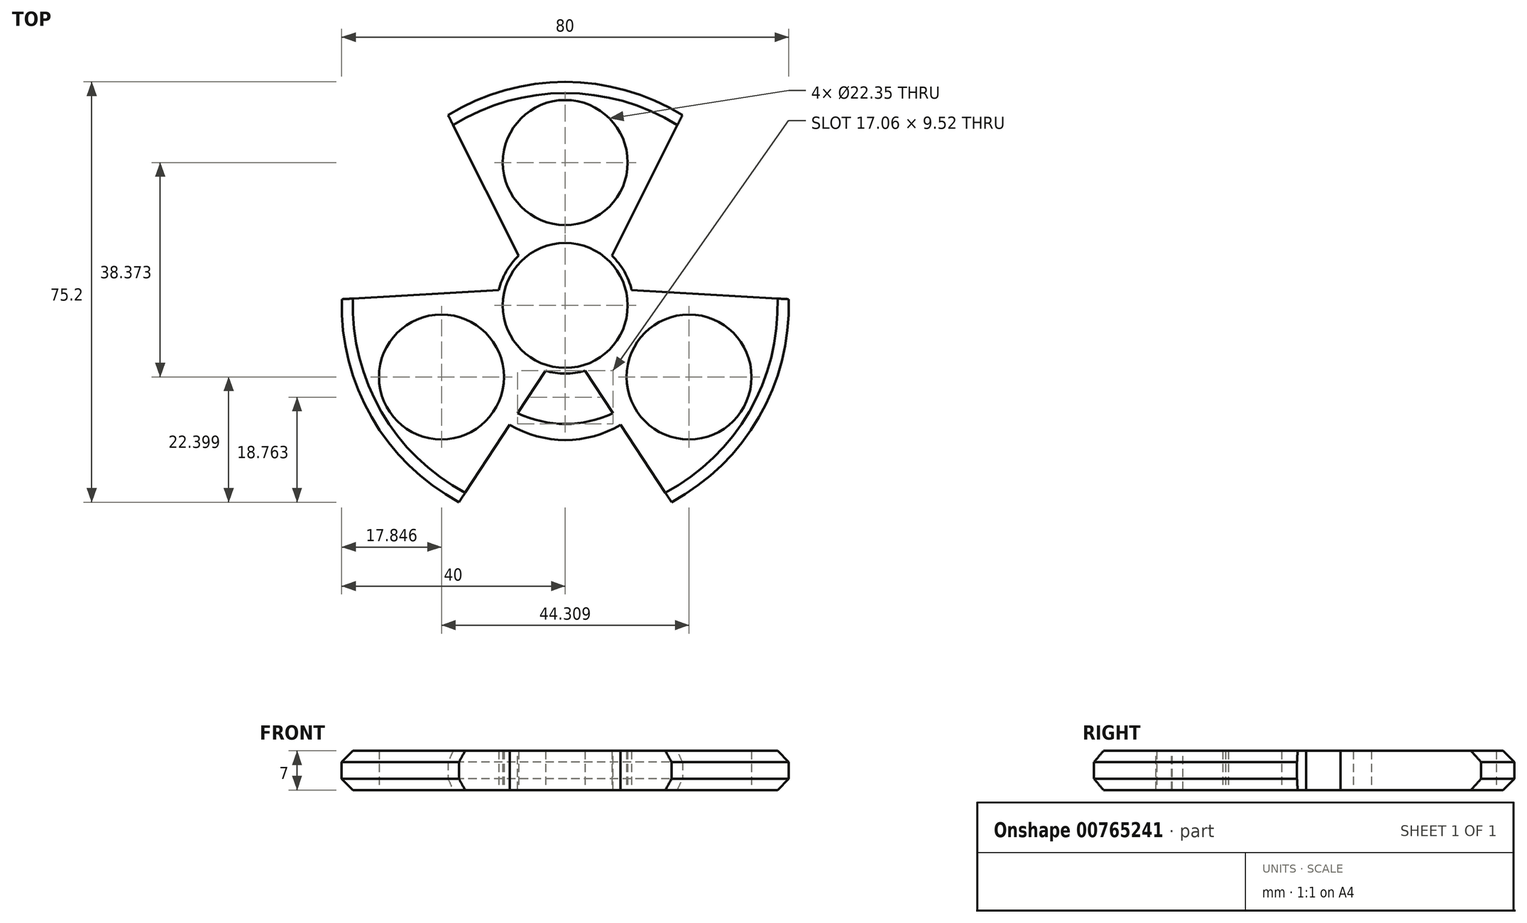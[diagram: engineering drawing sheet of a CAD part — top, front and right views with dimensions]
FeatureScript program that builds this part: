
annotation { "Feature Type Name" : "Feature", "Feature Type Description" : "" }
export const myFeature = defineFeature(function(context is Context, id is Id, definition is map)
    precondition{}
    {
        {
            var Q0;
            Q0=qCreatedBy(makeId("Top.planeOp"),FACE);
            var sketch = newSketch(context, id + "F0", { "sketchPlane" : qUnion([Q0])});
            skCircle(sketch, "E0", {"center": v(0, 0) * mm, "radius": 11.18 * mm});
            skCircle(sketch, "E1", {"center": v(0, 25.58) * mm, "radius": 11.18 * mm});
            skCircle(sketch, "E2", {"center": v(0, 0) * mm, "radius": 12.2 * mm});
            skLineSegment(sketch, "E3", {"start": v(-8.34, 8.9) * mm, "end": v(-20.97, 34.07) * mm});
            skLineSegment(sketch, "E4.MirrorCS", {"start": v(8.34, 8.9) * mm, "end": v(20.97, 34.07) * mm});
            skArc(sketch, "E5", {"start": v(20.97, 34.07) * mm, "mid": v(0, 40) * mm, "end": v(-20.97, 34.07) * mm});
            skSolve(sketch);
        }
        {
            var Q0;
            Q0 = qSketchRegion(id + "F0", true);
            extrude(context, id + "F1", {"entities" : qUnion([Q0]), "depth" : 7 * mm, "offsetDistance" : 25.4 * mm});
        }
        {
            var Q0;
            Q0=makeQuery(id+"F1.opExtrude","SWEPT_BODY",BODY,{"disambiguationData":[OSD([sQuery(id+"F0.wireOp",EDGE,"E0"),sQuery(id+"F0.wireOp",EDGE,"6LQZuzW2-BXmh-GNf9-c3Ea-PcEizYLKoVNa"),sQuery(id+"F0.wireOp",EDGE,"52de568f-3869-4a7f-bed3-dca6302ad32c0.MirrorCS"),sQuery(id+"F0.wireOp",EDGE,"f5ZPJVid-AG3l-EzfC-Y73m-c0DhcH7INsbp"),sQuery(id+"F0.wireOp",EDGE,"EpOvHbNq-JgKS-DAxY-9Kgq-gU8QQ25QF3dw")])]});
            var Q1;
            Q1=makeQuery(id+"F1.opExtrude","SWEPT_FACE",FACE,{"disambiguationData":[OSD([sQuery(id+"F0.wireOp",EDGE,"E2")])]});
            circularPattern(context, id + "F2", {"operationType" : NewBodyOperationType.ADD, "entities" : qUnion([Q0]), "axis" : qUnion([Q1]), "angle" : 360 * degree, "instanceCount" : 3, "equalSpace" : true});
        }
        {
            var Q0;
            {var subQ0=makeQuery(id+"F1.opExtrude","CAP_FACE",FACE,{"disambiguationData":[OSD([sQuery(id+"F0.wireOp",EDGE,"E0"),sQuery(id+"F0.wireOp",EDGE,"E1"),sQuery(id+"F0.wireOp",EDGE,"E2"),sQuery(id+"F0.wireOp",EDGE,"E3"),sQuery(id+"F0.wireOp",EDGE,"E4.MirrorCS"),sQuery(id+"F0.wireOp",EDGE,"E5")])],"isStart":false});Q0=makeQuery(id+"F2.boolean.opBoolean","MERGE",FACE,{"derivedFrom":[subQ0,makeQuery(id+"F2.opPattern","COPY",FACE,{"derivedFrom":subQ0,"instanceName":"1"}),makeQuery(id+"F2.opPattern","COPY",FACE,{"derivedFrom":subQ0,"instanceName":"2"})]});}
            var sketch = newSketch(context, id + "F3", { "sketchPlane" : qUnion([Q0])});
            skLineSegment(sketch, "E6", {"start": v(-11.28, -23.43) * mm, "end": v(-8.53, -19.25) * mm});
            skLineSegment(sketch, "E7", {"start": v(11.28, -23.43) * mm, "end": v(8.53, -19.25) * mm});
            skArc(sketch, "E8", {"start": v(-8.53, -19.25) * mm, "mid": v(0, -21.18) * mm, "end": v(8.53, -19.25) * mm});
            skArc(sketch, "E9", {"start": v(-9.9, -21.34) * mm, "mid": v(0, -24.07) * mm, "end": v(9.9, -21.34) * mm});
            skSolve(sketch);
        }
        {
            var Q0;
            Q0 = qSketchRegion(id + "F3", true);
            extrude(context, id + "F4", {"entities" : qUnion([Q0]), "operationType" : NewBodyOperationType.ADD, "oppositeDirection" : true, "depth" : 7 * mm, "offsetDistance" : 25.4 * mm});
        }
        {
            var Q0;
            Q0=makeQuery(id+"F2.opPattern","COPY",EDGE,{"derivedFrom":makeQuery(id+"F1.opExtrude","CAP_EDGE",EDGE,{"disambiguationData":[OSD([sQuery(id+"F0.wireOp",EDGE,"E5")])],"isStart":false}),"instanceName":"1"});
            var Q1;
            Q1=makeQuery(id+"F2.opPattern","COPY",EDGE,{"derivedFrom":makeQuery(id+"F1.opExtrude","CAP_EDGE",EDGE,{"disambiguationData":[OSD([sQuery(id+"F0.wireOp",EDGE,"E5")])],"isStart":true}),"instanceName":"1"});
            chamfer(context, id + "F5", {"entities" : qUnion([Q0, Q1]), "width" : 2 * mm, "tangentPropagation" : true});
        }
        {
            var Q0;
            Q0=makeQuery(id+"F2.opPattern","COPY",EDGE,{"derivedFrom":makeQuery(id+"F1.opExtrude","CAP_EDGE",EDGE,{"disambiguationData":[OSD([sQuery(id+"F0.wireOp",EDGE,"E5")])],"isStart":false}),"instanceName":"2"});
            var Q1;
            Q1=makeQuery(id+"F2.opPattern","COPY",EDGE,{"derivedFrom":makeQuery(id+"F1.opExtrude","CAP_EDGE",EDGE,{"disambiguationData":[OSD([sQuery(id+"F0.wireOp",EDGE,"E5")])],"isStart":true}),"instanceName":"2"});
            chamfer(context, id + "F6", {"entities" : qUnion([Q0, Q1]), "width" : 2 * mm, "tangentPropagation" : true});
        }
        {
            var Q0;
            Q0=makeQuery(id+"F1.opExtrude","CAP_EDGE",EDGE,{"disambiguationData":[OSD([sQuery(id+"F0.wireOp",EDGE,"E5")])],"isStart":false});
            var Q1;
            Q1=makeQuery(id+"F1.opExtrude","CAP_EDGE",EDGE,{"disambiguationData":[OSD([sQuery(id+"F0.wireOp",EDGE,"E5")])],"isStart":true});
            chamfer(context, id + "F7", {"entities" : qUnion([Q0, Q1]), "width" : 2 * mm, "tangentPropagation" : true});
        }
    });
